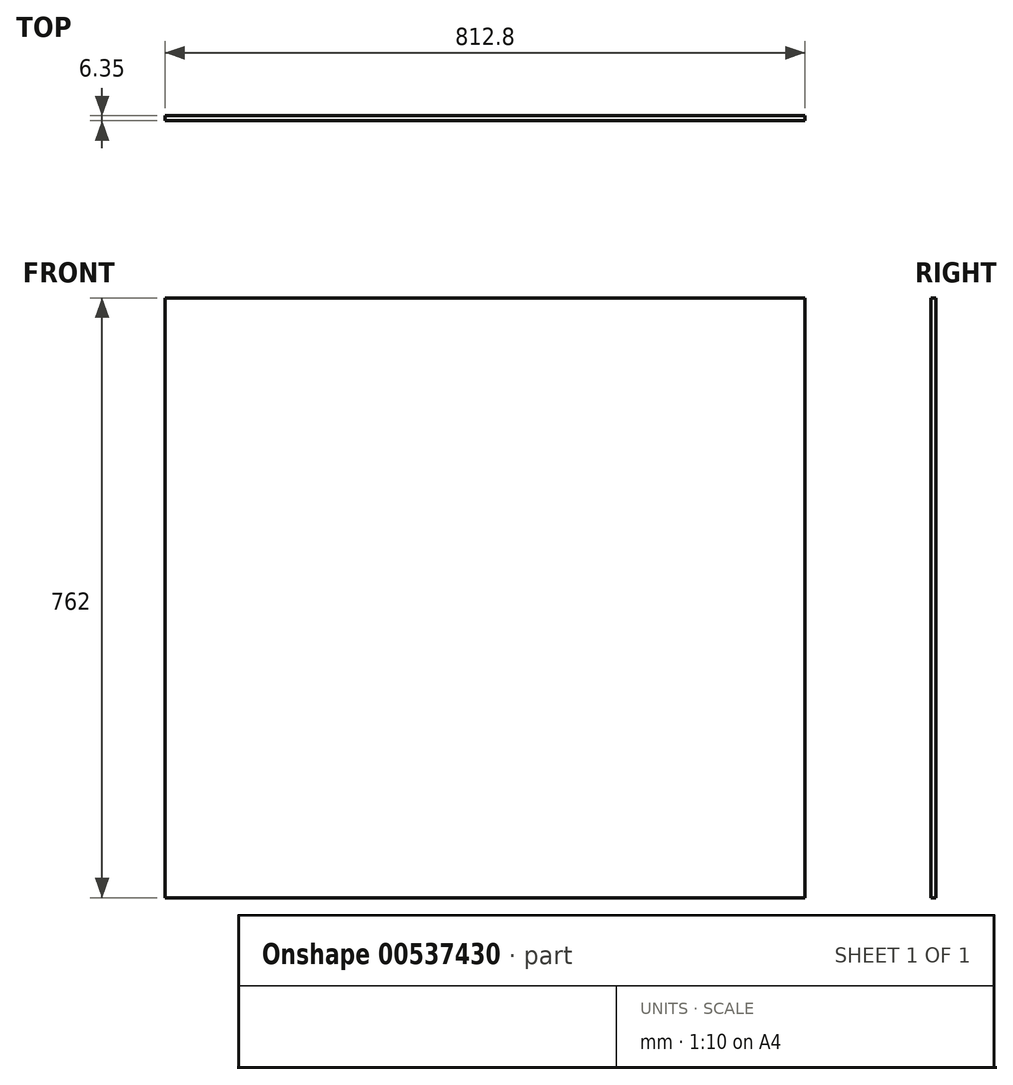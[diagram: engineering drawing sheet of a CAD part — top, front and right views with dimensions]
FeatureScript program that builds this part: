
annotation { "Feature Type Name" : "Feature", "Feature Type Description" : "" }
export const myFeature = defineFeature(function(context is Context, id is Id, definition is map)
    precondition{}
    {
        {
            var Q0;
            Q0=qCreatedBy(makeId("Front.planeOp"),FACE);
            var sketch = newSketch(context, id + "F0", { "sketchPlane" : qUnion([Q0])});
            skLineSegment(sketch, "E0.bottom", {"start": v(406.4, 381) * mm, "end": v(-406.4, 381) * mm});
            skLineSegment(sketch, "E0.top", {"start": v(406.4, -381) * mm, "end": v(-406.4, -381) * mm});
            skLineSegment(sketch, "E0.left", {"start": v(406.4, 381) * mm, "end": v(406.4, -381) * mm});
            skLineSegment(sketch, "E0.right", {"start": v(-406.4, 381) * mm, "end": v(-406.4, -381) * mm});
            skPoint(sketch, "E0.middle", {"position": v(0, 0) * mm});
            skSolve(sketch);
        }
        {
            var Q0;
            Q0=makeQuery(id+"F0.imprint","IMPRINT",FACE,{"disambiguationData":[TD([[makeQuery(id+"F0.imprint","IMPRINT",EDGE,{"derivedFrom":sQuery(id+"F0.wireOp",EDGE,"E0.bottom")}),1.0]])]});
            extrude(context, id + "F1", {"entities" : qUnion([Q0]), "depth" : 6.35 * mm, "offsetDistance" : 25.4 * mm});
        }
    });
